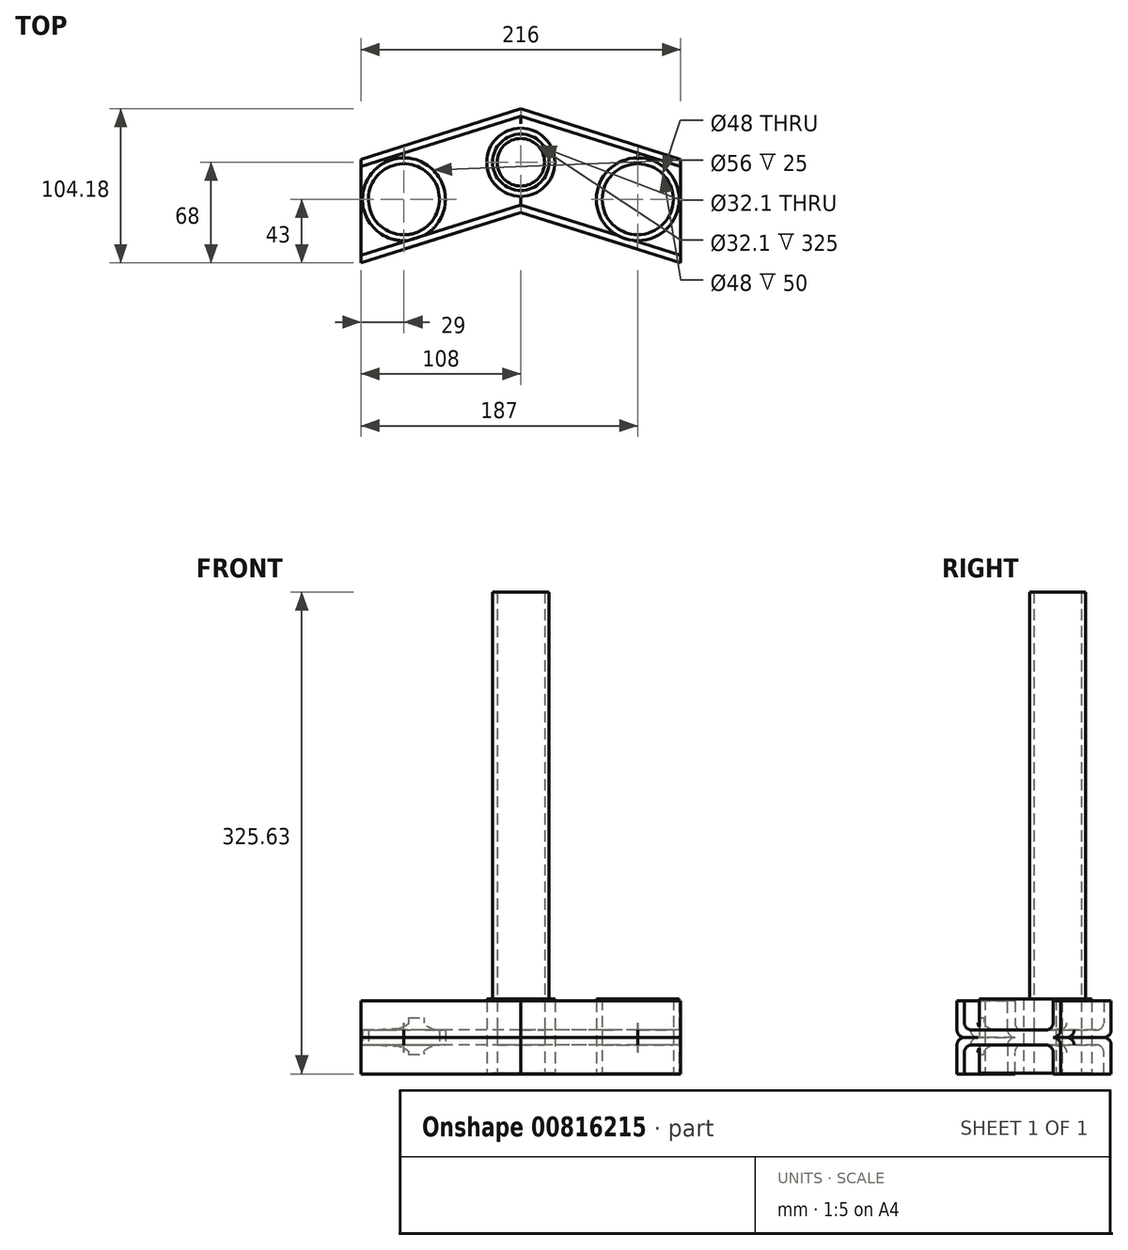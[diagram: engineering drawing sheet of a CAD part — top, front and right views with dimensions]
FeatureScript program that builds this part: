
annotation { "Feature Type Name" : "Feature", "Feature Type Description" : "" }
export const myFeature = defineFeature(function(context is Context, id is Id, definition is map)
    precondition{}
    {
        {
            var Q0;
            Q0=qCreatedBy(makeId("Top.planeOp"),FACE);
            var sketch = newSketch(context, id + "F0", { "sketchPlane" : qUnion([Q0])});
            skLineSegment(sketch, "E0", {"start": v(0, 0) * mm, "end": v(79, 0) * mm, "construction": true});
            skLineSegment(sketch, "E1", {"start": v(0, 0) * mm, "end": v(0, 25) * mm, "construction": true});
            skCircle(sketch, "E2", {"center": v(79, 0) * mm, "radius": 28 * mm});
            skCircle(sketch, "E3", {"center": v(79, 0) * mm, "radius": 24 * mm});
            skCircle(sketch, "E4", {"center": v(0, 25) * mm, "radius": 19.05 * mm});
            skCircle(sketch, "E5", {"center": v(0, 25) * mm, "radius": 23.05 * mm});
            skCircle(sketch, "E6.MirrorC", {"center": v(-79, 0) * mm, "radius": 28 * mm});
            skCircle(sketch, "E7.MirrorC", {"center": v(-79, 0) * mm, "radius": 24 * mm});
            skCircle(sketch, "E8", {"center": v(0, 25) * mm, "radius": 16.05 * mm});
            skLineSegment(sketch, "E9", {"start": v(0, 60.47) * mm, "end": v(108, 60.47) * mm, "construction": true});
            skLineSegment(sketch, "E10", {"start": v(108, 60.47) * mm, "end": v(108, -45.18) * mm, "construction": true});
            skLineSegment(sketch, "E11", {"start": v(0, 25) * mm, "end": v(79, 0) * mm});
            skLineSegment(sketch, "E12", {"start": v(79, 0) * mm, "end": v(108, -9.18) * mm});
            skLineSegment(sketch, "E13.MirrorCS", {"start": v(0, 25) * mm, "end": v(-79, 0) * mm});
            skLineSegment(sketch, "E14.MirrorCS", {"start": v(-79, 0) * mm, "end": v(-108, -9.18) * mm});
            skSolve(sketch);
        }
        {
            var Q0;
            Q0=makeQuery(id+"F0.imprint","IMPRINT",FACE,{"disambiguationData":[TD([[makeQuery(id+"F0.imprint","IMPRINT",EDGE,{"derivedFrom":sQuery(id+"F0.wireOp",EDGE,"E6.MirrorC")}),-1.0]])]});
            var Q1;
            Q1=makeQuery(id+"F0.imprint","IMPRINT",FACE,{"disambiguationData":[TD([[makeQuery(id+"F0.imprint","IMPRINT",EDGE,{"derivedFrom":sQuery(id+"F0.wireOp",EDGE,"E2")}),1.0]])]});
            extrude(context, id + "F1", {"entities" : qUnion([Q0, Q1]), "endBound" : BoundingType.SYMMETRIC, "depth" : 50 * mm, "offsetDistance" : 25 * mm});
        }
        {
            var Q0;
            {var subQ0=sQuery(id+"F0.wireOp",EDGE,"FZspJeiB-y2cj-0Xdk-k6OS-iXAF7RchaXki");var subQ1=sQuery(id+"F0.wireOp",EDGE,"E4");var subQ2=makeQuery(id+"F0.imprint","INTERSECT",VERTEX,{"derivedFrom":[subQ1,subQ0]});Q0=makeQuery(id+"F0.imprint","IMPRINT",FACE,{"disambiguationData":[TD([[makeQuery(id+"F0.imprint","IMPRINT",EDGE,{"disambiguationData":[TD([[subQ2,1.0]])],"derivedFrom":subQ1}),1.0]])]});}
            var Q1;
            {var subQ0=sQuery(id+"F0.wireOp",EDGE,"FZspJeiB-y2cj-0Xdk-k6OS-iXAF7RchaXki");var subQ1=sQuery(id+"F0.wireOp",EDGE,"E4");var subQ2=makeQuery(id+"F0.imprint","INTERSECT",VERTEX,{"derivedFrom":[subQ1,subQ0]});Q1=makeQuery(id+"F0.imprint","IMPRINT",FACE,{"disambiguationData":[TD([[makeQuery(id+"F0.imprint","IMPRINT",EDGE,{"disambiguationData":[TD([[subQ2,-1.0]])],"derivedFrom":subQ1}),1.0]])]});}
            extrude(context, id + "F2", {"entities" : qUnion([Q0, Q1]), "depth" : 300 * mm, "offsetDistance" : 25 * mm, "hasSecondDirection" : true, "secondDirectionOppositeDirection" : true, "secondDirectionDepth" : 25 * mm});
        }
        {
            var Q0;
            {var subQ0=sQuery(id+"F0.wireOp",EDGE,"FZspJeiB-y2cj-0Xdk-k6OS-iXAF7RchaXki");var subQ1=sQuery(id+"F0.wireOp",EDGE,"E4");var subQ2=makeQuery(id+"F0.imprint","INTERSECT",VERTEX,{"derivedFrom":[subQ1,subQ0]});Q0=makeQuery(id+"F0.imprint","IMPRINT",FACE,{"disambiguationData":[TD([[makeQuery(id+"F0.imprint","IMPRINT",EDGE,{"disambiguationData":[TD([[subQ2,-1.0]])],"derivedFrom":subQ1}),-1.0]])]});}
            var Q1;
            {var subQ0=sQuery(id+"F0.wireOp",EDGE,"FZspJeiB-y2cj-0Xdk-k6OS-iXAF7RchaXki");var subQ1=sQuery(id+"F0.wireOp",EDGE,"E4");var subQ2=makeQuery(id+"F0.imprint","INTERSECT",VERTEX,{"derivedFrom":[subQ1,subQ0]});Q1=makeQuery(id+"F0.imprint","IMPRINT",FACE,{"disambiguationData":[TD([[makeQuery(id+"F0.imprint","IMPRINT",EDGE,{"disambiguationData":[TD([[subQ2,1.0]])],"derivedFrom":subQ1}),-1.0]])]});}
            extrude(context, id + "F3", {"entities" : qUnion([Q0, Q1]), "operationType" : NewBodyOperationType.ADD, "endBound" : BoundingType.SYMMETRIC, "depth" : 50 * mm, "offsetDistance" : 25 * mm});
        }
        {
            var Q0;
            Q0=qCreatedBy(makeId("Right.planeOp"),FACE);
            cPlane(context, id + "F4", {"entities" : qUnion([Q0]), "cplaneType" : CPlaneType.OFFSET, "offset" : 108 * mm, "width" : 150 * mm, "height" : 150 * mm});
        }
        {
            var Q0;
            Q0=qCreatedBy(id+"F4.planeOp",FACE);
            var sketch = newSketch(context, id + "F5", { "sketchPlane" : qUnion([Q0])});
            skLineSegment(sketch, "E15", {"start": v(27, 4) * mm, "end": v(27, 23.63) * mm});
            skLineSegment(sketch, "E16", {"start": v(27, 23.63) * mm, "end": v(22, 23.63) * mm});
            skLineSegment(sketch, "E17", {"start": v(22, 23.63) * mm, "end": v(22, 9) * mm});
            skLineSegment(sketch, "E18", {"start": v(17, 4) * mm, "end": v(-8, 4) * mm});
            skArc(sketch, "E19.filletArc", {"start": v(17, 4) * mm, "mid": v(20.54, 5.47) * mm, "end": v(22, 9) * mm});
            skArc(sketch, "E20.filletArc", {"start": v(22, -1) * mm, "mid": v(25.54, 0.47) * mm, "end": v(27, 4) * mm});
            skLineSegment(sketch, "E21.MirrorCS", {"start": v(-33, 4) * mm, "end": v(-8, 4) * mm});
            skArc(sketch, "E22.MirrorCS", {"start": v(-33, 4) * mm, "mid": v(-36.54, 5.47) * mm, "end": v(-38, 9) * mm});
            skArc(sketch, "E23.MirrorCS", {"start": v(-38, -1) * mm, "mid": v(-41.54, 0.47) * mm, "end": v(-43, 4) * mm});
            skLineSegment(sketch, "E24.MirrorCS", {"start": v(-43, 4) * mm, "end": v(-43, 23.63) * mm});
            skLineSegment(sketch, "E25.MirrorCS", {"start": v(-38, 23.63) * mm, "end": v(-38, 9) * mm});
            skLineSegment(sketch, "E26.MirrorCS", {"start": v(-43, 23.63) * mm, "end": v(-38, 23.63) * mm});
            skLineSegment(sketch, "E27.MirrorCS", {"start": v(17, -6) * mm, "end": v(-8, -6) * mm});
            skLineSegment(sketch, "E28.MirrorCS", {"start": v(27, -25.63) * mm, "end": v(22, -25.63) * mm});
            skLineSegment(sketch, "E29.MirrorCS", {"start": v(27, -6) * mm, "end": v(27, -25.63) * mm});
            skLineSegment(sketch, "E30.MirrorCS", {"start": v(22, -25.63) * mm, "end": v(22, -11) * mm});
            skArc(sketch, "E31.MirrorCS", {"start": v(22, -1) * mm, "mid": v(25.54, -2.46) * mm, "end": v(27, -6) * mm});
            skArc(sketch, "E32.MirrorCS", {"start": v(17, -6) * mm, "mid": v(20.54, -7.46) * mm, "end": v(22, -11) * mm});
            skLineSegment(sketch, "E33.MirrorCS", {"start": v(-33, -6) * mm, "end": v(-8, -6) * mm});
            skArc(sketch, "E34.MirrorCS", {"start": v(-38, -1) * mm, "mid": v(-41.54, -2.46) * mm, "end": v(-43, -6) * mm});
            skArc(sketch, "E35.MirrorCS", {"start": v(-33, -6) * mm, "mid": v(-36.54, -7.46) * mm, "end": v(-38, -11) * mm});
            skLineSegment(sketch, "E36.MirrorCS", {"start": v(-38, -25.63) * mm, "end": v(-38, -11) * mm});
            skLineSegment(sketch, "E37.MirrorCS", {"start": v(-43, -25.63) * mm, "end": v(-38, -25.63) * mm});
            skLineSegment(sketch, "E38.MirrorCS", {"start": v(-43, -6) * mm, "end": v(-43, -25.63) * mm});
            skSolve(sketch);
        }
        {
            var Q0;
            Q0=makeQuery(id+"F5.imprint","IMPRINT",FACE,{"disambiguationData":[TD([[makeQuery(id+"F5.imprint","IMPRINT",EDGE,{"derivedFrom":sQuery(id+"F5.wireOp",EDGE,"E15")}),1.0]])]});
            var Q1;
            Q1=sQuery(id+"F0.wireOp",EDGE,"E12");
            var Q2;
            Q2=sQuery(id+"F0.wireOp",EDGE,"E11");
            var Q3;
            Q3=sQuery(id+"F0.wireOp",EDGE,"E13.MirrorCS");
            var Q4;
            Q4=sQuery(id+"F0.wireOp",EDGE,"E14.MirrorCS");
            sweep(context, id + "F6", {"profiles" : qUnion([Q0]), "path" : qUnion([Q1, Q2, Q3, Q4]), "keepProfileOrientation" : true});
        }
        {
            var Q0;
            {var subQ0=sQuery(id+"F0.wireOp",EDGE,"E11");var subQ1=sQuery(id+"F0.wireOp",EDGE,"E3");var subQ2=makeQuery(id+"F0.imprint","INTERSECT",VERTEX,{"derivedFrom":[subQ1,subQ0]});Q0=makeQuery(id+"F0.imprint","IMPRINT",FACE,{"disambiguationData":[TD([[makeQuery(id+"F0.imprint","IMPRINT",EDGE,{"disambiguationData":[TD([[subQ2,1.0]])],"derivedFrom":subQ1}),1.0]])]});}
            var Q1;
            {var subQ0=sQuery(id+"F0.wireOp",EDGE,"E11");var subQ1=sQuery(id+"F0.wireOp",EDGE,"E3");var subQ2=makeQuery(id+"F0.imprint","INTERSECT",VERTEX,{"derivedFrom":[subQ1,subQ0]});Q1=makeQuery(id+"F0.imprint","IMPRINT",FACE,{"disambiguationData":[TD([[makeQuery(id+"F0.imprint","IMPRINT",EDGE,{"disambiguationData":[TD([[subQ2,-1.0]])],"derivedFrom":subQ1}),1.0]])]});}
            var Q2;
            {var subQ0=sQuery(id+"F0.wireOp",EDGE,"E11");var subQ1=sQuery(id+"F0.wireOp",EDGE,"E8");var subQ2=makeQuery(id+"F0.imprint","INTERSECT",VERTEX,{"derivedFrom":[subQ1,subQ0]});Q2=makeQuery(id+"F0.imprint","IMPRINT",FACE,{"disambiguationData":[TD([[makeQuery(id+"F0.imprint","IMPRINT",EDGE,{"disambiguationData":[TD([[subQ2,-1.0]])],"derivedFrom":subQ1}),1.0]])]});}
            var Q3;
            {var subQ0=sQuery(id+"F0.wireOp",EDGE,"E11");var subQ1=sQuery(id+"F0.wireOp",EDGE,"E8");var subQ2=makeQuery(id+"F0.imprint","INTERSECT",VERTEX,{"derivedFrom":[subQ1,subQ0]});Q3=makeQuery(id+"F0.imprint","IMPRINT",FACE,{"disambiguationData":[TD([[makeQuery(id+"F0.imprint","IMPRINT",EDGE,{"disambiguationData":[TD([[subQ2,1.0]])],"derivedFrom":subQ1}),1.0]])]});}
            var Q4;
            {var subQ0=sQuery(id+"F0.wireOp",EDGE,"E13.MirrorCS");var subQ1=sQuery(id+"F0.wireOp",EDGE,"E7.MirrorC");var subQ2=makeQuery(id+"F0.imprint","INTERSECT",VERTEX,{"derivedFrom":[subQ1,subQ0]});Q4=makeQuery(id+"F0.imprint","IMPRINT",FACE,{"disambiguationData":[TD([[makeQuery(id+"F0.imprint","IMPRINT",EDGE,{"disambiguationData":[TD([[subQ2,1.0]])],"derivedFrom":subQ1}),-1.0]])]});}
            var Q5;
            {var subQ0=sQuery(id+"F0.wireOp",EDGE,"E13.MirrorCS");var subQ1=sQuery(id+"F0.wireOp",EDGE,"E7.MirrorC");var subQ2=makeQuery(id+"F0.imprint","INTERSECT",VERTEX,{"derivedFrom":[subQ1,subQ0]});Q5=makeQuery(id+"F0.imprint","IMPRINT",FACE,{"disambiguationData":[TD([[makeQuery(id+"F0.imprint","IMPRINT",EDGE,{"disambiguationData":[TD([[subQ2,-1.0]])],"derivedFrom":subQ1}),-1.0]])]});}
            var Q6;
            Q6=sQuery(id+"F0.wireOp",EDGE,"E7.MirrorC");
            extrude(context, id + "F7", {"entities" : qUnion([Q0, Q1, Q2, Q3, Q4, Q5]), "operationType" : NewBodyOperationType.REMOVE, "surfaceEntities" : qUnion([Q6]), "endBound" : BoundingType.SYMMETRIC, "depth" : 25 * mm, "offsetDistance" : 25 * mm});
        }
    });
